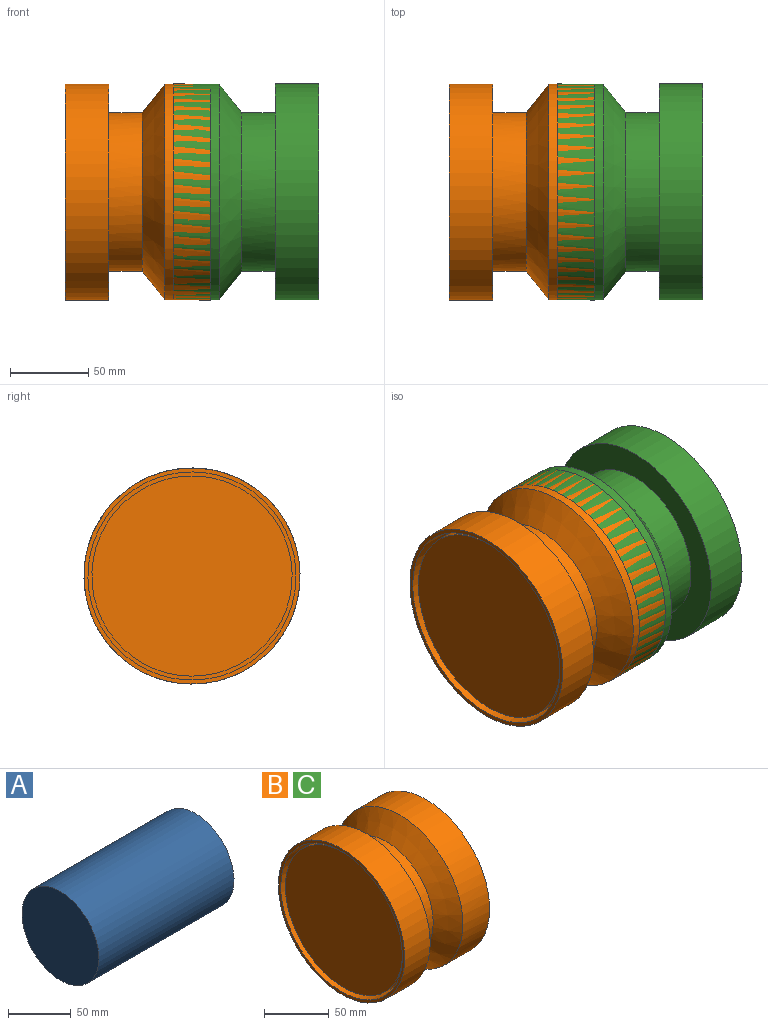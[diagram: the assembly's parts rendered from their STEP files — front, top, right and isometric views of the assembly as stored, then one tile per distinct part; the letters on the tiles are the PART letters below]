
ASSEMBLY  parts=3 mates=3
PART A: 3 faces, bbox 152.4x86.7x86.7 mm
  f0: cylinder r=43.35mm len=152.4mm, axis (-1,0,0), area 41505.4mm2, adj f1,f2
  f1: plane 86.69x86.69mm, normal (1,0,0), area 5902.4mm2, adj f0
  f2: plane 86.69x86.69mm, normal (-1,0,0), area 5902.4mm2, adj f0
PART B: 25 faces, bbox 93.1x138.5x138.5 mm
  f0: cylinder r=50.96mm len=101.93mm, axis (1,0,0), area 6893.1mm2, adj f1,f5
  f1: cone r=50mm half-angle=51.8deg, axis (1,0,0), area 8792.5mm2, adj f0,f2
  f2: cylinder r=69.25mm len=138.5mm, axis (-1,0,0), area 12692.8mm2, adj f1,f3
  f3: plane 138.5x138.5mm, normal (1,0,0), area 3133.1mm2, adj f2,f9
  f4: cylinder r=69.25mm len=138.5mm, axis (-1,0,0), area 12156.7mm2, adj f5,f6
  f5: plane 138.5x138.5mm, normal (1,0,0), area 6905.4mm2, adj f0,f4
  f6: plane 138.5x138.5mm, normal (-1,0,0), area 1084.9mm2, adj f4,f17
  f7: cylinder r=43.34mm len=86.69mm, axis (1,0,0), area 8944.3mm2, adj f8,f11
  f8: cone r=45.28mm half-angle=51.8deg, axis (1,0,0), area 7677.8mm2, adj f7,f9
  f9: cylinder r=61.63mm len=123.26mm, axis (-1,0,0), area 9864.8mm2, adj f3,f8
  f10: cylinder r=61.63mm len=123.26mm, axis (-1,0,0), area 5901.3mm2, adj f11,f12
  f11: plane 123.26x123.26mm, normal (-1,0,0), area 6030mm2, adj f7,f10
  f12: plane 123.26x123.26mm, normal (1,0,0), area 11932mm2, adj f10
  f13: cylinder r=48.42mm len=96.85mm, axis (1,0,0), area 7697.2mm2, adj f14,f18
  f14: cone r=48.42mm half-angle=51.8deg, axis (1,0,0), area 8420.9mm2, adj f13,f15
  f15: cylinder r=66.71mm len=133.42mm, axis (-1,0,0), area 10646.2mm2, adj f14,f16
  f16: plane 133.42x133.42mm, normal (-1,0,0), area 1044.4mm2, adj f15,f21
  f17: cylinder r=66.71mm len=133.42mm, axis (-1,0,0), area 10646.2mm2, adj f6,f18
  f18: plane 133.42x133.42mm, normal (-1,0,0), area 6613.6mm2, adj f13,f17
  f19: cylinder r=45.88mm len=91.77mm, axis (1,0,0), area 8381mm2, adj f20,f23
  f20: cone r=46.85mm half-angle=51.8deg, axis (1,0,0), area 8049.3mm2, adj f19,f21
  f21: cylinder r=64.17mm len=128.34mm, axis (-1,0,0), area 9744.1mm2, adj f16,f20
  f22: cylinder r=64.17mm len=128.34mm, axis (-1,0,0), area 8192.7mm2, adj f23,f24
  f23: plane 128.34x128.34mm, normal (1,0,0), area 6321.8mm2, adj f19,f22
  f24: plane 128.34x128.34mm, normal (-1,0,0), area 12935.8mm2, adj f22
PART C: same geometry as B
PLACE A rot(axis=(-1,0,0),2.9deg) t=(122.78,172.47,28.21)mm
PLACE B rot(axis=(-1,0,0),2.9deg) t=(150.25,174.95,76.57)mm
PLACE C rot(axis=(0,1,-0.03),180deg) t=(247.7,169.99,-20.15)mm
MATE cylindrical B.f0 <-> A.f0  axis (1,0,0) through (122.78,172.47,28.21)mm
MATE cylindrical C.f0 <-> A.f0  axis (-1,0,0) through (275.18,172.47,28.21)mm
MATE cylindrical B.f0 <-> A.f0  axis (1,0,0) through (122.78,172.47,28.21)mm
